# Revit family: Layout-Teknion-Zones_Open_Lounge_02-R2022
name_source: partatom
category: Furniture Systems
units: mm (PartAtom-declared; Revit-internal decimal feet)

## family parameters
Always vertical = Yes
Cut with Voids When Loaded = No
OmniClass Number = 23.40.70.14.64.21
OmniClass Title = Systems Furniture
Part Type = Normal
Room Calculation Point = No
Round Connector Dimension = Use Diameter
Shared = No
Work Plane-Based = No

## types (1)
- Open Lounge 02
    Apparent Load = 21 VA
    Apparent Load Note = Wiht Floor Lamp = 21 VA - Without Floor Lamp = 0 V
    Assembly Code = E2020200
    Connector Description = Power Connector
    Default Elevation = 0' - 0"
    Depth = 9' - 0 3/8"
    Description = 8'  9 5/16" x 9'  0 3/8"
    Height = 5' - 6 25/32"
    Manufacturer = Teknion
    Manufacturer Fax = 416.661.4586
    Model = Open Lounge Zone 02
    Product Line = Zones
    Product Page URL = http://teknionplanningtool.com
    Series = Zones
    Sustainability Data = http://www.teknion.com
    URL = http://www.teknion.com
    Voltage = 120 V
    Voltage Note = With Floor Lamp = 120 V - Without Floor Lamp = 0 V
    Warranty = http://www.teknion.com
    Width = 8' - 9 5/16"

## geometry (parser evidence)
native form markers: Blend x241, Sweep x52
no freeform markers — native parametric forms only
